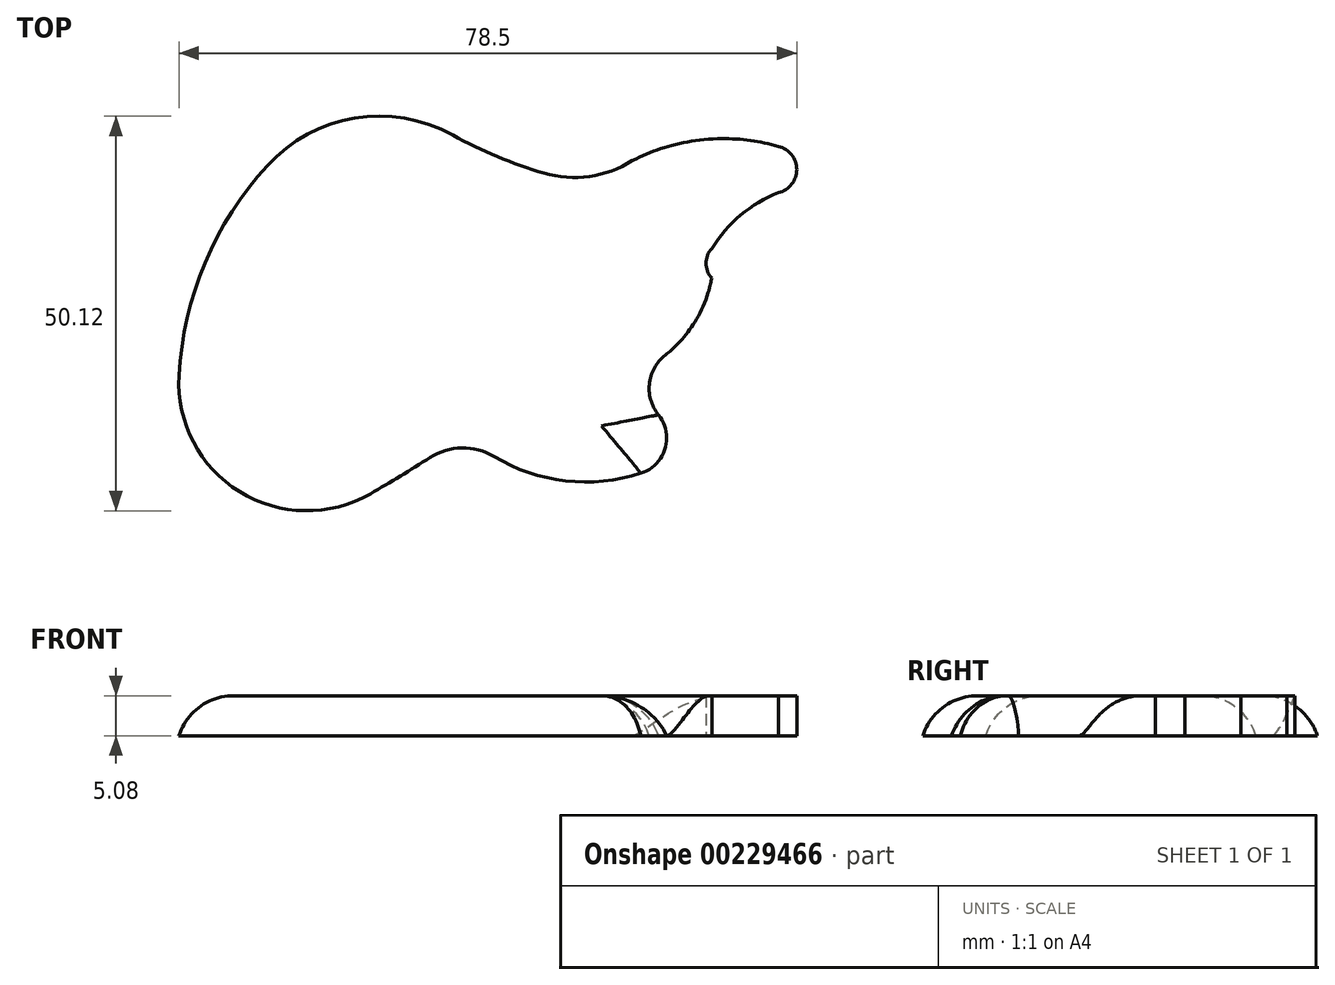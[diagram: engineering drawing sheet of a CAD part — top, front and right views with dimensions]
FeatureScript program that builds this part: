
annotation { "Feature Type Name" : "Feature", "Feature Type Description" : "" }
export const myFeature = defineFeature(function(context is Context, id is Id, definition is map)
    precondition{}
    {
        {
            var Q0;
            Q0=qCreatedBy(makeId("Top.planeOp"),FACE);
            var sketch = newSketch(context, id + "F0", { "sketchPlane" : qUnion([Q0])});
            skArc(sketch, "E0", {"start": v(43.43, 65.42) * mm, "mid": v(30.98, 67.56) * mm, "end": v(19.88, 61.55) * mm});
            skArc(sketch, "E1", {"start": v(19.88, 61.55) * mm, "mid": v(11.95, 49.17) * mm, "end": v(8.65, 34.85) * mm});
            skArc(sketch, "E2", {"start": v(8.65, 34.85) * mm, "mid": v(16.35, 20.12) * mm, "end": v(32.97, 19.85) * mm});
            skArc(sketch, "E3", {"start": v(32.97, 19.85) * mm, "mid": v(36.78, 22.1) * mm, "end": v(40.53, 24.46) * mm});
            skArc(sketch, "E4", {"start": v(40.53, 24.46) * mm, "mid": v(44.57, 25.69) * mm, "end": v(48.65, 24.6) * mm});
            skArc(sketch, "E5", {"start": v(48.65, 24.6) * mm, "mid": v(57.76, 21.5) * mm, "end": v(67.33, 22.47) * mm});
            skArc(sketch, "E6", {"start": v(67.33, 22.47) * mm, "mid": v(70.38, 25.6) * mm, "end": v(69.55, 29.88) * mm});
            skArc(sketch, "E7", {"start": v(69.55, 29.88) * mm, "mid": v(68.43, 34) * mm, "end": v(70.65, 37.65) * mm});
            skArc(sketch, "E8", {"start": v(43.43, 65.42) * mm, "mid": v(49.1, 62.69) * mm, "end": v(55.02, 60.59) * mm});
            skArc(sketch, "E9", {"start": v(55.02, 60.59) * mm, "mid": v(60.77, 60.17) * mm, "end": v(66.2, 62.15) * mm});
            skArc(sketch, "E10", {"start": v(84.8, 63.97) * mm, "mid": v(75.32, 64.85) * mm, "end": v(66.2, 62.15) * mm});
            skArc(sketch, "E11", {"start": v(84.8, 58.11) * mm, "mid": v(87.13, 61.04) * mm, "end": v(84.8, 63.97) * mm});
            skArc(sketch, "E12", {"start": v(84.8, 58.11) * mm, "mid": v(79.98, 55.25) * mm, "end": v(76.32, 51) * mm});
            skArc(sketch, "E13", {"start": v(76.32, 51) * mm, "mid": v(75.6, 49.13) * mm, "end": v(76.32, 47.27) * mm});
            skArc(sketch, "E14", {"start": v(70.65, 37.65) * mm, "mid": v(74.33, 41.96) * mm, "end": v(76.32, 47.27) * mm});
            skSolve(sketch);
        }
        {
            var Q0;
            Q0=makeQuery(id+"F0.imprint","IMPRINT",FACE,{"disambiguationData":[TD([[makeQuery(id+"F0.imprint","IMPRINT",EDGE,{"derivedFrom":sQuery(id+"F0.wireOp",EDGE,"E0")}),1.0]])]});
            extrude(context, id + "F1", {"entities" : qUnion([Q0]), "depth" : 5.08 * mm});
        }
        {
            var Q0;
            Q0=makeQuery(id+"F1.opExtrude","CAP_EDGE",EDGE,{"disambiguationData":[OSD([sQuery(id+"F0.wireOp",EDGE,"E2")])],"isStart":false});
            fillet(context, id + "F2", {"entities" : qUnion([Q0]), "radius" : 7.36 * mm, "tangentPropagation" : true, "allowEdgeOverflow" : false});
        }
    });
